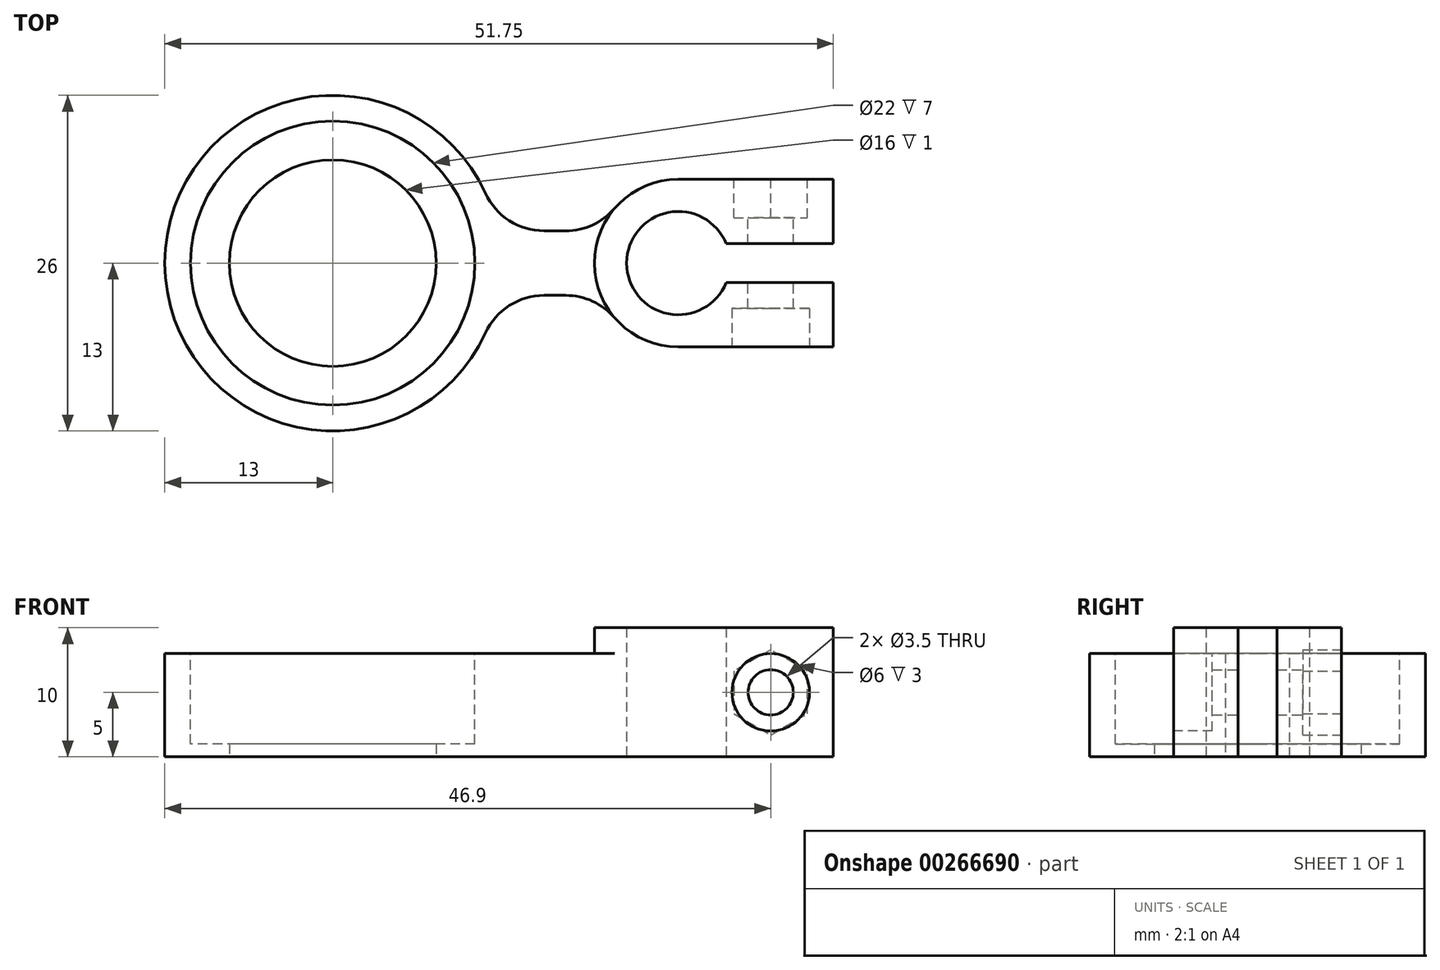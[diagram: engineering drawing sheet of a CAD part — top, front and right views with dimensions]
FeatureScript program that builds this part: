
annotation { "Feature Type Name" : "Feature", "Feature Type Description" : "" }
export const myFeature = defineFeature(function(context is Context, id is Id, definition is map)
    precondition{}
    {
        {
            var Q0;
            Q0=qCreatedBy(makeId("Top.planeOp"),FACE);
            var sketch = newSketch(context, id + "F0", { "sketchPlane" : qUnion([Q0])});
            skArc(sketch, "E0", {"start": v(3.7, 1.5) * mm, "mid": v(-4, 0) * mm, "end": v(3.7, -1.5) * mm});
            skCircle(sketch, "E1", {"center": v(-26.75, 0) * mm, "radius": 8 * mm});
            skArc(sketch, "E2", {"start": v(-6, -2.5) * mm, "mid": v(-3.6, -5.4) * mm, "end": v(0, -6.5) * mm});
            skArc(sketch, "E3", {"start": v(-14, 2.5) * mm, "mid": v(-39.75, 0) * mm, "end": v(-14, -2.5) * mm});
            skLineSegment(sketch, "E4", {"start": v(0, 6.5) * mm, "end": v(12, 6.5) * mm});
            skLineSegment(sketch, "E5", {"start": v(12, 6.5) * mm, "end": v(12, 1.5) * mm});
            skLineSegment(sketch, "E6", {"start": v(12, 1.5) * mm, "end": v(3.7, 1.5) * mm});
            skLineSegment(sketch, "E7", {"start": v(0, -6.5) * mm, "end": v(12, -6.5) * mm});
            skLineSegment(sketch, "E8", {"start": v(12, -6.5) * mm, "end": v(12, -1.5) * mm});
            skLineSegment(sketch, "E9", {"start": v(12, -1.5) * mm, "end": v(3.7, -1.5) * mm});
            skLineSegment(sketch, "E10.bottom", {"start": v(-6, 2.5) * mm, "end": v(-14, 2.5) * mm});
            skLineSegment(sketch, "E10.top", {"start": v(-6, -2.5) * mm, "end": v(-14, -2.5) * mm});
            skArc(sketch, "E11.trimOffspring", {"start": v(0, 6.5) * mm, "mid": v(-3.6, 5.4) * mm, "end": v(-6, 2.5) * mm});
            skSolve(sketch);
        }
        {
            var Q0;
            Q0=qSketchRegion(id+"F0",true);
            extrude(context, id + "F1", {"entities" : qUnion([Q0]), "depth" : 10 * mm});
        }
        {
            var Q0;
            Q0=makeQuery(id+"F1.opExtrude","CAP_FACE",FACE,{"disambiguationData":[OSD([sQuery(id+"F0.wireOp",EDGE,"E0"),sQuery(id+"F0.wireOp",EDGE,"E1"),sQuery(id+"F0.wireOp",EDGE,"E2"),sQuery(id+"F0.wireOp",EDGE,"E3"),sQuery(id+"F0.wireOp",EDGE,"E4"),sQuery(id+"F0.wireOp",EDGE,"E5"),sQuery(id+"F0.wireOp",EDGE,"E6"),sQuery(id+"F0.wireOp",EDGE,"E7"),sQuery(id+"F0.wireOp",EDGE,"E8"),sQuery(id+"F0.wireOp",EDGE,"E9"),sQuery(id+"F0.wireOp",EDGE,"E10.bottom"),sQuery(id+"F0.wireOp",EDGE,"E10.top"),sQuery(id+"F0.wireOp",EDGE,"E11.trimOffspring")])],"isStart":false});
            var sketch = newSketch(context, id + "F2", { "sketchPlane" : qUnion([Q0])});
            skCircle(sketch, "E12", {"center": v(-26.75, 0) * mm, "radius": 11 * mm});
            skSolve(sketch);
        }
        {
            var Q0;
            Q0=qSketchRegion(id+"F2",true);
            extrude(context, id + "F3", {"entities" : qUnion([Q0]), "operationType" : NewBodyOperationType.REMOVE, "oppositeDirection" : true, "depth" : 9 * mm});
        }
        {
            var Q0;
            Q0=makeQuery(id+"F1.opExtrude","CAP_FACE",FACE,{"disambiguationData":[OSD([sQuery(id+"F0.wireOp",EDGE,"E0"),sQuery(id+"F0.wireOp",EDGE,"E1"),sQuery(id+"F0.wireOp",EDGE,"E2"),sQuery(id+"F0.wireOp",EDGE,"E3"),sQuery(id+"F0.wireOp",EDGE,"E4"),sQuery(id+"F0.wireOp",EDGE,"E5"),sQuery(id+"F0.wireOp",EDGE,"E6"),sQuery(id+"F0.wireOp",EDGE,"E7"),sQuery(id+"F0.wireOp",EDGE,"E8"),sQuery(id+"F0.wireOp",EDGE,"E9"),sQuery(id+"F0.wireOp",EDGE,"E10.bottom"),sQuery(id+"F0.wireOp",EDGE,"E10.top"),sQuery(id+"F0.wireOp",EDGE,"E11.trimOffspring")])],"isStart":false});
            var sketch = newSketch(context, id + "F4", { "sketchPlane" : qUnion([Q0])});
            skArc(sketch, "E13", {"start": v(-14, 2.5) * mm, "mid": v(-39.75, 0) * mm, "end": v(-14, -2.5) * mm});
            skArc(sketch, "E14", {"start": v(-6, 2.5) * mm, "mid": v(-6.5, 0) * mm, "end": v(-6, -2.5) * mm});
            skLineSegment(sketch, "E15", {"start": v(-6, 2.5) * mm, "end": v(-14, 2.5) * mm});
            skLineSegment(sketch, "E16", {"start": v(-6, -2.5) * mm, "end": v(-14, -2.5) * mm});
            skSolve(sketch);
        }
        {
            var Q0;
            Q0=qSketchRegion(id+"F4",true);
            extrude(context, id + "F5", {"entities" : qUnion([Q0]), "operationType" : NewBodyOperationType.REMOVE, "oppositeDirection" : true, "depth" : 2 * mm});
        }
        {
            var Q0;
            Q0=makeQuery(id+"F1.opExtrude","SWEPT_FACE",FACE,{"disambiguationData":[OSD([sQuery(id+"F0.wireOp",EDGE,"E4")])]});
            var sketch = newSketch(context, id + "F6", { "sketchPlane" : qUnion([Q0])});
            skCircle(sketch, "E17.cCircle", {"center": v(-7.15, 5) * mm, "radius": 2.85 * mm, "construction": true});
            skPoint(sketch, "E17.cCircle.centerSnap0", {"position": v(-12, 5) * mm});
            skLineSegment(sketch, "E17.0", {"start": v(-10, 3.35) * mm, "end": v(-10, 6.65) * mm});
            skLineSegment(sketch, "E17.1", {"start": v(-10, 6.65) * mm, "end": v(-7.15, 8.3) * mm});
            skLineSegment(sketch, "E17.2", {"start": v(-7.15, 8.3) * mm, "end": v(-4.3, 6.65) * mm});
            skLineSegment(sketch, "E17.3", {"start": v(-4.3, 6.65) * mm, "end": v(-4.3, 3.35) * mm});
            skLineSegment(sketch, "E17.4", {"start": v(-4.3, 3.35) * mm, "end": v(-7.15, 1.7) * mm});
            skLineSegment(sketch, "E17.5", {"start": v(-7.15, 1.7) * mm, "end": v(-10, 3.35) * mm});
            skPoint(sketch, "E17.0.midPoint", {"position": v(-10, 5) * mm});
            skSolve(sketch);
        }
        {
            var Q0;
            Q0=qSketchRegion(id+"F6",true);
            extrude(context, id + "F7", {"entities" : qUnion([Q0]), "operationType" : NewBodyOperationType.REMOVE, "oppositeDirection" : true, "depth" : 3 * mm});
        }
        {
            var Q0;
            Q0=makeQuery(id+"F1.opExtrude","SWEPT_FACE",FACE,{"disambiguationData":[OSD([sQuery(id+"F0.wireOp",EDGE,"E4")])]});
            var sketch = newSketch(context, id + "F8", { "sketchPlane" : qUnion([Q0])});
            skCircle(sketch, "E18", {"center": v(-7.15, 5) * mm, "radius": 1.75 * mm});
            skPoint(sketch, "E18.centerSnap0", {"position": v(-4.3, 5) * mm});
            skSolve(sketch);
        }
        {
            var Q0;
            Q0=qSketchRegion(id+"F8",true);
            extrude(context, id + "F9", {"entities" : qUnion([Q0]), "operationType" : NewBodyOperationType.REMOVE, "endBound" : BoundingType.THROUGH_ALL, "oppositeDirection" : true, "depth" : 25 * mm});
        }
        {
            var Q0;
            Q0=makeQuery(id+"F1.opExtrude","SWEPT_FACE",FACE,{"disambiguationData":[OSD([sQuery(id+"F0.wireOp",EDGE,"E7")])]});
            var sketch = newSketch(context, id + "F10", { "sketchPlane" : qUnion([Q0])});
            skCircle(sketch, "E19", {"center": v(7.15, 5) * mm, "radius": 3 * mm});
            skSolve(sketch);
        }
        {
            var Q0;
            Q0=qSketchRegion(id+"F10",true);
            extrude(context, id + "F11", {"entities" : qUnion([Q0]), "operationType" : NewBodyOperationType.REMOVE, "oppositeDirection" : true, "depth" : 3 * mm});
        }
        {
            var Q0;
            Q0=makeQuery(id+"F1.opExtrude","SWEPT_EDGE",EDGE,{"disambiguationData":[OSD([sQuery(id+"F0.wireOp",EDGE,"E2"),sQuery(id+"F0.wireOp",EDGE,"E10.top")])]});
            var Q1;
            Q1=makeQuery(id+"F1.opExtrude","SWEPT_EDGE",EDGE,{"disambiguationData":[OSD([sQuery(id+"F0.wireOp",EDGE,"E3"),sQuery(id+"F0.wireOp",EDGE,"E10.top")])]});
            var Q2;
            Q2=makeQuery(id+"F1.opExtrude","SWEPT_EDGE",EDGE,{"disambiguationData":[OSD([sQuery(id+"F0.wireOp",EDGE,"E3"),sQuery(id+"F0.wireOp",EDGE,"E10.bottom")])]});
            var Q3;
            Q3=makeQuery(id+"F1.opExtrude","SWEPT_EDGE",EDGE,{"disambiguationData":[OSD([sQuery(id+"F0.wireOp",EDGE,"E10.bottom"),sQuery(id+"F0.wireOp",EDGE,"E11.trimOffspring")])]});
            fillet(context, id + "F12", {"entities" : qUnion([Q0, Q1, Q2, Q3]), "radius" : 5 * mm, "tangentPropagation" : true, "allowEdgeOverflow" : false});
        }
    });
